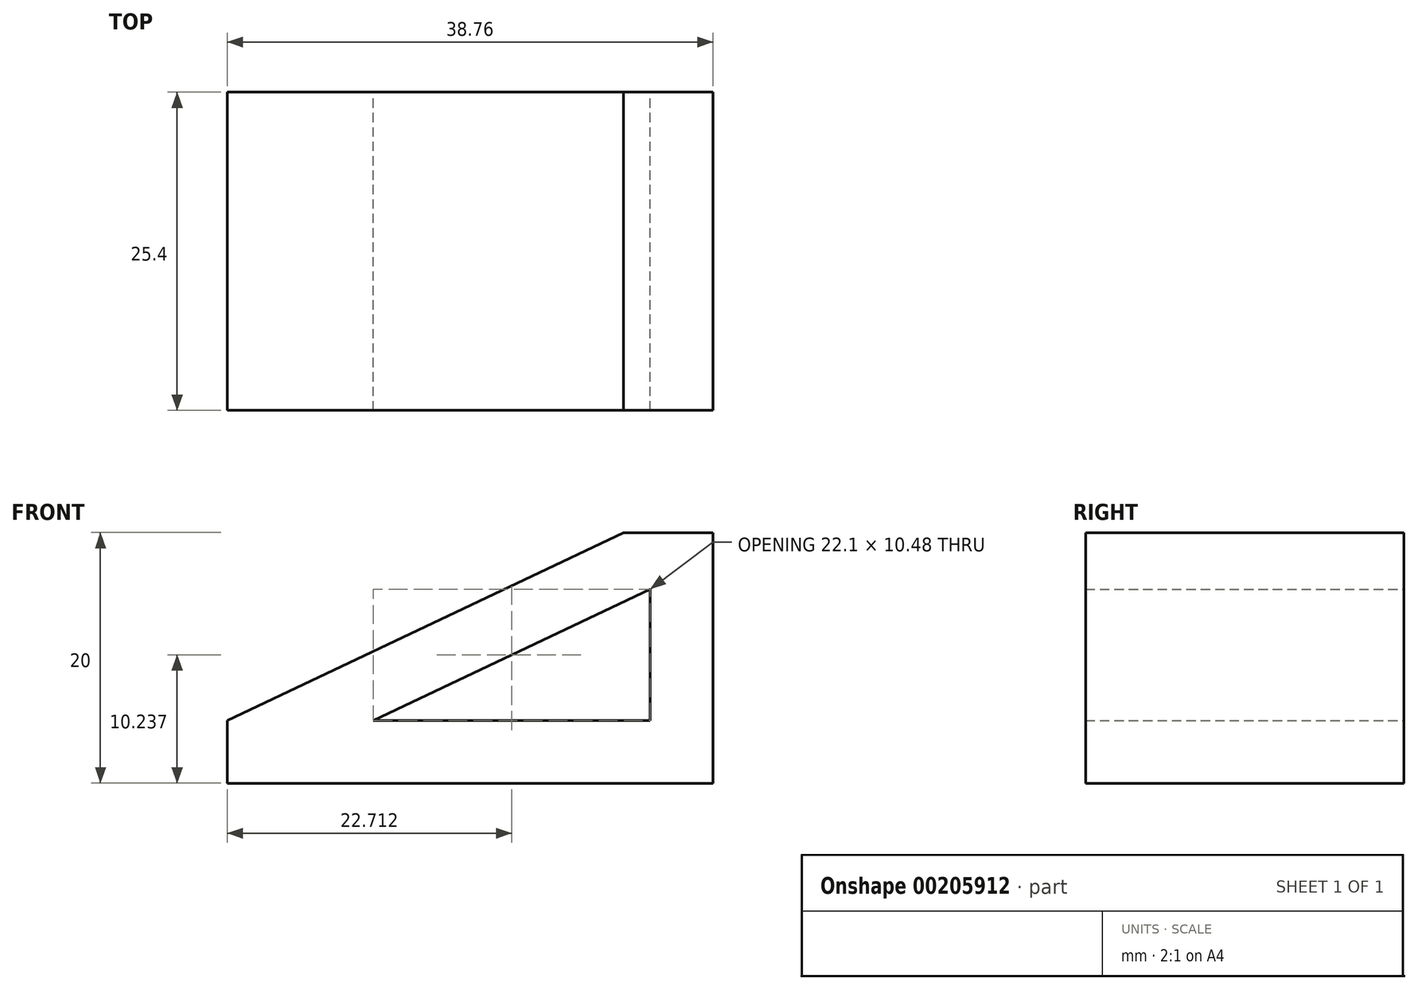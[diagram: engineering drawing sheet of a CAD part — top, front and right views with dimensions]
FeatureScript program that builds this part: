
annotation { "Feature Type Name" : "Feature", "Feature Type Description" : "" }
export const myFeature = defineFeature(function(context is Context, id is Id, definition is map)
    precondition{}
    {
        {
            var Q0;
            Q0=qCreatedBy(makeId("Front.planeOp"),FACE);
            var sketch = newSketch(context, id + "F0", { "sketchPlane" : qUnion([Q0])});
            skLineSegment(sketch, "E0", {"start": v(-15.18, 19.92) * mm, "end": v(-37.28, 9.44) * mm});
            skLineSegment(sketch, "E1", {"start": v(-15.18, 19.92) * mm, "end": v(-15.18, 9.44) * mm});
            skLineSegment(sketch, "E2", {"start": v(-15.18, 19.92) * mm, "end": v(-17.32, 24.44) * mm});
            skLineSegment(sketch, "E3", {"start": v(-17.32, 24.44) * mm, "end": v(-10.18, 24.44) * mm});
            skLineSegment(sketch, "E4", {"start": v(-10.18, 24.44) * mm, "end": v(-10.18, 9.44) * mm});
            skLineSegment(sketch, "E5", {"start": v(-10.18, 9.44) * mm, "end": v(-10.18, 4.44) * mm});
            skLineSegment(sketch, "E6", {"start": v(-48.94, 4.44) * mm, "end": v(-48.94, 9.44) * mm});
            skLineSegment(sketch, "E7", {"start": v(-48.94, 9.44) * mm, "end": v(-17.32, 24.44) * mm});
            skLineSegment(sketch, "E8", {"start": v(-48.94, 9.44) * mm, "end": v(-37.28, 9.44) * mm});
            skLineSegment(sketch, "E9", {"start": v(-15.18, 9.44) * mm, "end": v(-10.18, 4.44) * mm});
            skLineSegment(sketch, "E10", {"start": v(-37.28, 9.44) * mm, "end": v(-15.18, 9.44) * mm});
            skLineSegment(sketch, "E11", {"start": v(-48.94, 4.44) * mm, "end": v(-10.18, 4.44) * mm});
            skSolve(sketch);
        }
        {
            var Q0;
            Q0 = qSketchRegion(id + "F0", true);
            extrude(context, id + "F1", {"entities" : qUnion([Q0]), "depth" : 25.4 * mm});
        }
    });
